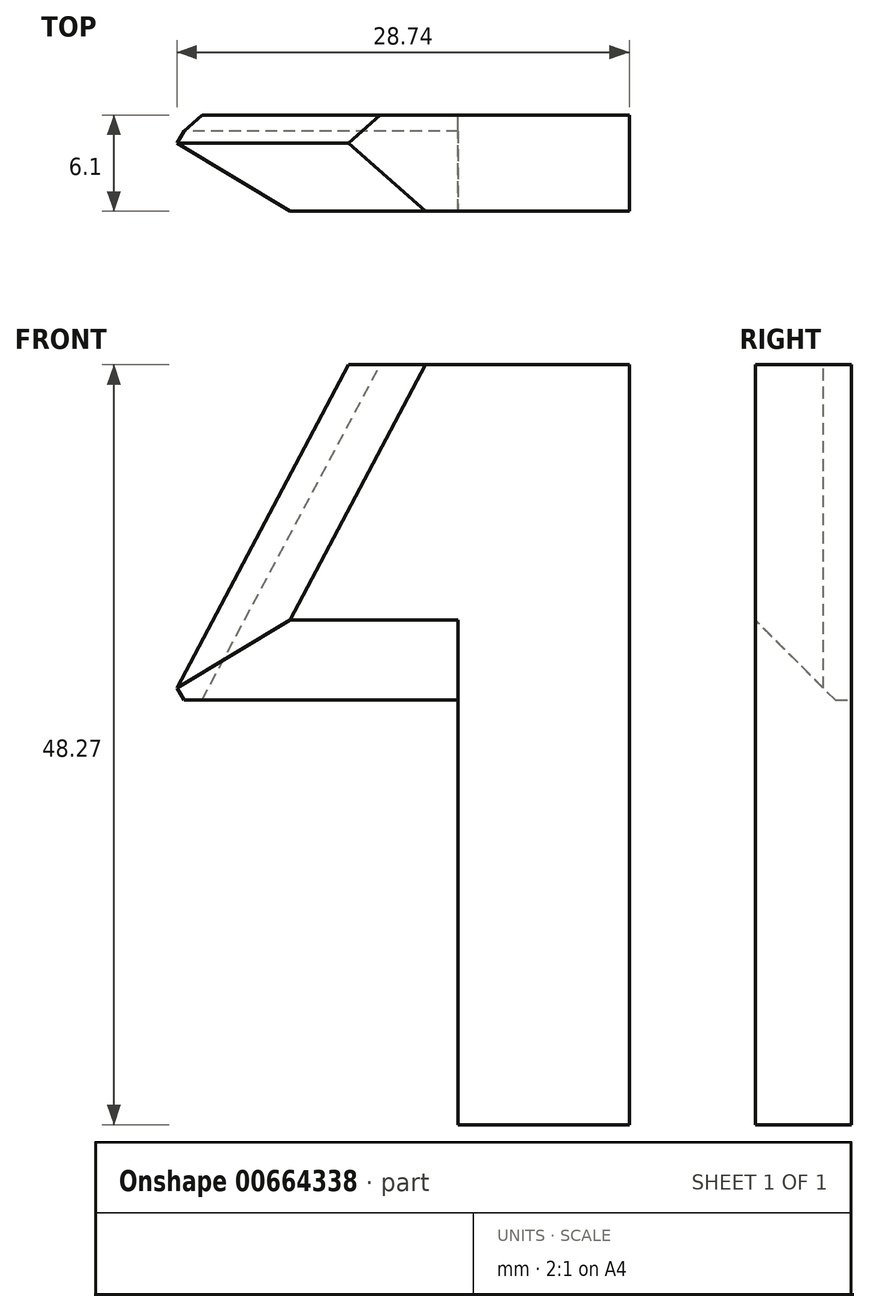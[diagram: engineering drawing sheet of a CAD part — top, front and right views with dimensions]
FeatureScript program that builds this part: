
annotation { "Feature Type Name" : "Feature", "Feature Type Description" : "" }
export const myFeature = defineFeature(function(context is Context, id is Id, definition is map)
    precondition{}
    {
        {
            var Q0;
            Q0=qCreatedBy(makeId("Front.planeOp"),FACE);
            var sketch = newSketch(context, id + "F0", { "sketchPlane" : qUnion([Q0])});
            skLineSegment(sketch, "E0", {"start": v(0, 64.8) * mm, "end": v(0, -48.27) * mm});
            skLineSegment(sketch, "E1", {"start": v(0, -48.27) * mm, "end": v(-10.87, -48.27) * mm});
            skLineSegment(sketch, "E2", {"start": v(-10.87, -48.27) * mm, "end": v(-10.87, -21.3) * mm});
            skLineSegment(sketch, "E3", {"start": v(-10.87, -21.3) * mm, "end": v(-30, -21.3) * mm});
            skLineSegment(sketch, "E4", {"start": v(-30, -21.3) * mm, "end": v(-18.7, 0) * mm});
            skLineSegment(sketch, "E5", {"start": v(-18.7, 0) * mm, "end": v(0, 0) * mm});
            skLineSegment(sketch, "E6", {"start": v(0, 0) * mm, "end": v(-18.7, 0) * mm});
            skLineSegment(sketch, "E7", {"start": v(-18.7, 56.96) * mm, "end": v(-18.7, 0) * mm});
            skLineSegment(sketch, "E8", {"start": v(-18.7, 56.96) * mm, "end": v(0, 64.8) * mm});
            skSolve(sketch);
        }
        {
            var Q0;
            {var subQ2=sQuery(id+"F0.wireOp",EDGE,"E6");Q0=makeQuery(id+"F0.imprint","IMPRINT",FACE,{"disambiguationData":[TD([[makeQuery(id+"F0.imprint","IMPRINT",EDGE,{"derivedFrom":subQ2}),-1.0]])]});}
            var Q1;
            {var subQ0=sQuery(id+"F0.wireOp",EDGE,"E1");Q1=makeQuery(id+"F0.imprint","IMPRINT",FACE,{"disambiguationData":[TD([[makeQuery(id+"F0.imprint","IMPRINT",EDGE,{"derivedFrom":subQ0}),-1.0]])]});}
            extrude(context, id + "F1", {"entities" : qUnion([Q0, Q1]), "depth" : 6.1 * mm, "offsetDistance" : 25.4 * mm});
        }
        {
            var Q0;
            Q0=makeQuery(id+"F1.opExtrude","CAP_EDGE",EDGE,{"disambiguationData":[OSD([sQuery(id+"F0.wireOp",EDGE,"E7")])],"isStart":false});
            var Q1;
            Q1=makeQuery(id+"F1.opExtrude","CAP_EDGE",EDGE,{"disambiguationData":[OSD([sQuery(id+"F0.wireOp",EDGE,"E4")])],"isStart":false});
            var Q2;
            Q2=makeQuery(id+"F1.opExtrude","CAP_EDGE",EDGE,{"disambiguationData":[OSD([sQuery(id+"F0.wireOp",EDGE,"E8")])],"isStart":false});
            var Q3;
            Q3=makeQuery(id+"F1.opExtrude","CAP_EDGE",EDGE,{"disambiguationData":[OSD([sQuery(id+"F0.wireOp",EDGE,"E3")])],"isStart":false});
            var Q4;
            Q4=makeQuery(id+"F1.opExtrude","CAP_EDGE",EDGE,{"disambiguationData":[OSD([sQuery(id+"F0.wireOp",EDGE,"E8")])],"isStart":true});
            chamfer(context, id + "F2", {"entities" : qUnion([Q0, Q1, Q2, Q3, Q4]), "width" : 5.08 * mm, "tangentPropagation" : true});
        }
        {
            var Q0;
            Q0=makeQuery(id+"F1.opExtrude","CAP_EDGE",EDGE,{"disambiguationData":[OSD([sQuery(id+"F0.wireOp",EDGE,"E7")])],"isStart":false});
            var Q1;
            Q1=makeQuery(id+"F1.opExtrude","CAP_EDGE",EDGE,{"disambiguationData":[OSD([sQuery(id+"F0.wireOp",EDGE,"E4")])],"isStart":false});
            var Q2;
            Q2=makeQuery(id+"F1.opExtrude","CAP_EDGE",EDGE,{"disambiguationData":[OSD([sQuery(id+"F0.wireOp",EDGE,"E8")])],"isStart":false});
            var Q3;
            Q3=makeQuery(id+"F1.opExtrude","CAP_EDGE",EDGE,{"disambiguationData":[OSD([sQuery(id+"F0.wireOp",EDGE,"E8")])],"isStart":true});
            var Q4;
            Q4=makeQuery(id+"F1.opExtrude","CAP_EDGE",EDGE,{"disambiguationData":[OSD([sQuery(id+"F0.wireOp",EDGE,"E7")])],"isStart":true});
            var Q5;
            Q5=makeQuery(id+"F1.opExtrude","CAP_EDGE",EDGE,{"disambiguationData":[OSD([sQuery(id+"F0.wireOp",EDGE,"E4")])],"isStart":true});
            chamfer(context, id + "F3", {"entities" : qUnion([Q0, Q1, Q2, Q3, Q4, Q5]), "width" : 2.54 * mm, "tangentPropagation" : true});
        }
    });
